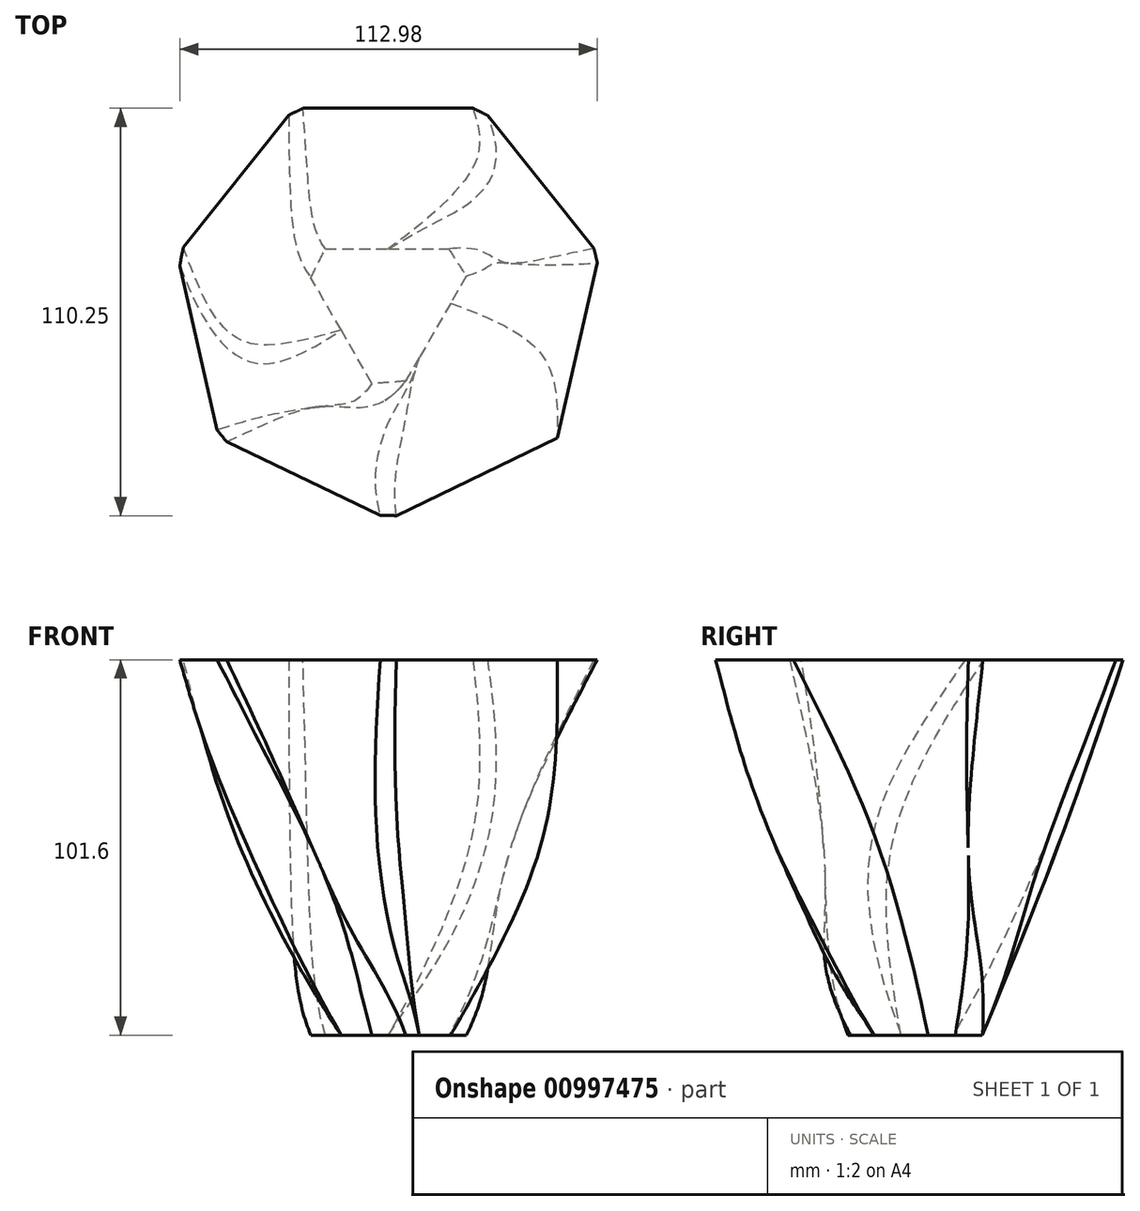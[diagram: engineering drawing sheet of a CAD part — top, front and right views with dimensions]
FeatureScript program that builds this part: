
annotation { "Feature Type Name" : "Feature", "Feature Type Description" : "" }
export const myFeature = defineFeature(function(context is Context, id is Id, definition is map)
    precondition{}
    {
        {
            var Q0;
            Q0=qCreatedBy(makeId("Top.planeOp"),FACE);
            var sketch = newSketch(context, id + "F0", { "sketchPlane" : qUnion([Q0])});
            skCircle(sketch, "E0.cCircle", {"center": v(0, 0) * mm, "radius": 14.66 * mm, "construction": true});
            skLineSegment(sketch, "E0.0", {"start": v(-25.4, 14.66) * mm, "end": v(25.4, 14.66) * mm});
            skLineSegment(sketch, "E0.1", {"start": v(25.4, 14.66) * mm, "end": v(0, -29.33) * mm});
            skLineSegment(sketch, "E0.2", {"start": v(0, -29.33) * mm, "end": v(-25.4, 14.66) * mm});
            skPoint(sketch, "E0.0.midPoint", {"position": v(0, 14.66) * mm});
            skSolve(sketch);
        }
        {
            var Q0;
            Q0=qCreatedBy(makeId("Top.planeOp"),FACE);
            cPlane(context, id + "F1", {"entities" : qUnion([Q0]), "cplaneType" : CPlaneType.OFFSET, "offset" : 50.8 * mm, "width" : 152.4 * mm, "height" : 152.4 * mm});
        }
        {
            var Q0;
            Q0=qCreatedBy(id+"F1.planeOp",FACE);
            var sketch = newSketch(context, id + "F2", { "sketchPlane" : qUnion([Q0])});
            skCircle(sketch, "E1.cCircle", {"center": v(0, 0) * mm, "radius": 34.96 * mm, "construction": true});
            skLineSegment(sketch, "E1.0", {"start": v(-25.4, 34.96) * mm, "end": v(25.4, 34.96) * mm});
            skLineSegment(sketch, "E1.1", {"start": v(25.4, 34.96) * mm, "end": v(41.1, -13.35) * mm});
            skLineSegment(sketch, "E1.2", {"start": v(41.1, -13.35) * mm, "end": v(0, -43.21) * mm});
            skLineSegment(sketch, "E1.3", {"start": v(0, -43.21) * mm, "end": v(-41.1, -13.35) * mm});
            skLineSegment(sketch, "E1.4", {"start": v(-41.1, -13.35) * mm, "end": v(-25.4, 34.96) * mm});
            skPoint(sketch, "E1.0.midPoint", {"position": v(0, 34.96) * mm});
            skSolve(sketch);
        }
        {
            var Q0;
            Q0=qCreatedBy(id+"F1.planeOp",FACE);
            cPlane(context, id + "F3", {"entities" : qUnion([Q0]), "cplaneType" : CPlaneType.OFFSET, "offset" : 50.8 * mm, "width" : 152.4 * mm, "height" : 152.4 * mm});
        }
        {
            var Q0;
            Q0=qCreatedBy(id+"F3.planeOp",FACE);
            var sketch = newSketch(context, id + "F4", { "sketchPlane" : qUnion([Q0])});
            skCircle(sketch, "E2.cCircle", {"center": v(0, 0) * mm, "radius": 52.74 * mm, "construction": true});
            skLineSegment(sketch, "E2.0", {"start": v(-25.4, 52.74) * mm, "end": v(25.4, 52.74) * mm});
            skLineSegment(sketch, "E2.1", {"start": v(25.4, 52.74) * mm, "end": v(57.07, 13.03) * mm});
            skLineSegment(sketch, "E2.2", {"start": v(57.07, 13.03) * mm, "end": v(45.77, -36.5) * mm});
            skLineSegment(sketch, "E2.3", {"start": v(45.77, -36.5) * mm, "end": v(0, -58.54) * mm});
            skLineSegment(sketch, "E2.4", {"start": v(0, -58.54) * mm, "end": v(-45.77, -36.5) * mm});
            skLineSegment(sketch, "E2.5", {"start": v(-45.77, -36.5) * mm, "end": v(-57.07, 13.03) * mm});
            skLineSegment(sketch, "E2.6", {"start": v(-57.07, 13.03) * mm, "end": v(-25.4, 52.74) * mm});
            skPoint(sketch, "E2.0.midPoint", {"position": v(0, 52.74) * mm});
            skSolve(sketch);
        }
        {
            var Q0;
            Q0=makeQuery(id+"F0.imprint","IMPRINT",FACE,{"disambiguationData":[TD([[makeQuery(id+"F0.imprint","IMPRINT",EDGE,{"derivedFrom":sQuery(id+"F0.wireOp",EDGE,"E0.0")}),-1.0]])]});
            var Q1;
            Q1=makeQuery(id+"F2.imprint","IMPRINT",FACE,{"disambiguationData":[TD([[makeQuery(id+"F2.imprint","IMPRINT",EDGE,{"derivedFrom":sQuery(id+"F2.wireOp",EDGE,"E1.0")}),-1.0]])]});
            var Q2;
            Q2=makeQuery(id+"F4.imprint","IMPRINT",FACE,{"disambiguationData":[TD([[makeQuery(id+"F4.imprint","IMPRINT",EDGE,{"derivedFrom":sQuery(id+"F4.wireOp",EDGE,"E2.0")}),-1.0]])]});
            loft(context, id + "F5", {"sheetProfilesArray" : [{ "sheetProfileEntities" : qUnion([Q0]) }, { "sheetProfileEntities" : qUnion([Q1]) }, { "sheetProfileEntities" : qUnion([Q2]) }]});
        }
        {
            var Q0;
            Q0=makeQuery(id+"F5.opLoft","SWEPT_EDGE",EDGE,{"disambiguationData":[OSD([sQuery(id+"F0.wireOp",EDGE,"E0.0"),sQuery(id+"F0.wireOp",EDGE,"E0.2"),sQuery(id+"F2.wireOp",EDGE,"E1.0"),sQuery(id+"F2.wireOp",EDGE,"E1.4"),sQuery(id+"F4.wireOp",EDGE,"E2.0"),sQuery(id+"F4.wireOp",EDGE,"E2.6")])]});
            var Q1;
            Q1=makeQuery(id+"F5.opLoft","SWEPT_EDGE",EDGE,{"disambiguationData":[OSD([sQuery(id+"F0.wireOp",EDGE,"E0.2"),sQuery(id+"F2.wireOp",EDGE,"E1.4"),sQuery(id+"F4.wireOp",EDGE,"E2.0"),sQuery(id+"F4.wireOp",EDGE,"E2.5"),sQuery(id+"F4.wireOp",EDGE,"E2.6")])]});
            var Q2;
            Q2=makeQuery(id+"F5.opLoft","SWEPT_EDGE",EDGE,{"disambiguationData":[OSD([sQuery(id+"F0.wireOp",EDGE,"E0.2"),sQuery(id+"F2.wireOp",EDGE,"E1.4"),sQuery(id+"F4.wireOp",EDGE,"E2.4"),sQuery(id+"F4.wireOp",EDGE,"E2.5"),sQuery(id+"F4.wireOp",EDGE,"E2.6")])]});
            var Q3;
            Q3=makeQuery(id+"F5.opLoft","SWEPT_EDGE",EDGE,{"disambiguationData":[OSD([sQuery(id+"F0.wireOp",EDGE,"E0.2"),sQuery(id+"F2.wireOp",EDGE,"E1.3"),sQuery(id+"F2.wireOp",EDGE,"E1.4"),sQuery(id+"F4.wireOp",EDGE,"E2.3"),sQuery(id+"F4.wireOp",EDGE,"E2.4"),sQuery(id+"F4.wireOp",EDGE,"E2.5")])]});
            var Q4;
            Q4=makeQuery(id+"F5.opLoft","SWEPT_EDGE",EDGE,{"disambiguationData":[OSD([sQuery(id+"F0.wireOp",EDGE,"E0.2"),sQuery(id+"F2.wireOp",EDGE,"E1.2"),sQuery(id+"F2.wireOp",EDGE,"E1.3"),sQuery(id+"F4.wireOp",EDGE,"E2.2"),sQuery(id+"F4.wireOp",EDGE,"E2.3"),sQuery(id+"F4.wireOp",EDGE,"E2.4")])]});
            var Q5;
            Q5=makeQuery(id+"F5.opLoft","SWEPT_EDGE",EDGE,{"disambiguationData":[OSD([sQuery(id+"F0.wireOp",EDGE,"E0.1"),sQuery(id+"F0.wireOp",EDGE,"E0.2"),sQuery(id+"F2.wireOp",EDGE,"E1.1"),sQuery(id+"F2.wireOp",EDGE,"E1.2"),sQuery(id+"F4.wireOp",EDGE,"E2.1"),sQuery(id+"F4.wireOp",EDGE,"E2.2")])]});
            var Q6;
            Q6=makeQuery(id+"F5.opLoft","SWEPT_EDGE",EDGE,{"disambiguationData":[OSD([sQuery(id+"F0.wireOp",EDGE,"E0.0"),sQuery(id+"F0.wireOp",EDGE,"E0.1"),sQuery(id+"F2.wireOp",EDGE,"E1.0"),sQuery(id+"F2.wireOp",EDGE,"E1.1"),sQuery(id+"F4.wireOp",EDGE,"E2.0"),sQuery(id+"F4.wireOp",EDGE,"E2.1")])]});
            chamfer(context, id + "F6", {"entities" : qUnion([Q0, Q1, Q2, Q3, Q4, Q5, Q6]), "width" : 5.08 * mm, "tangentPropagation" : true});
        }
    });
